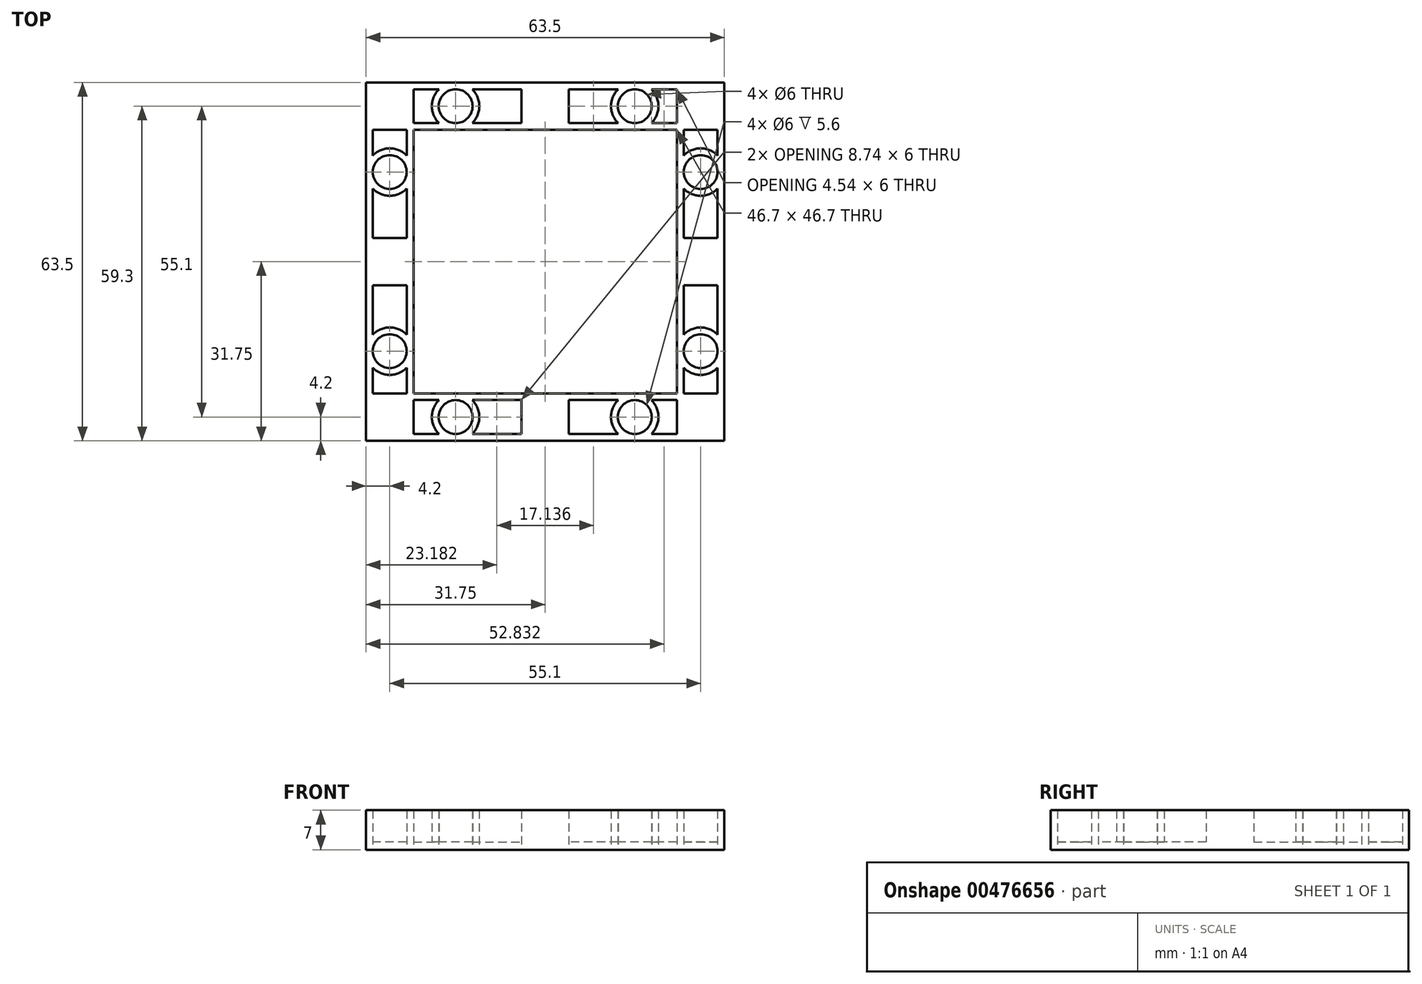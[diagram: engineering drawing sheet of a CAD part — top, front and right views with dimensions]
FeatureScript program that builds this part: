
annotation { "Feature Type Name" : "Feature", "Feature Type Description" : "" }
export const myFeature = defineFeature(function(context is Context, id is Id, definition is map)
    precondition{}
    {
        {
            var Q0;
            Q0=qCreatedBy(makeId("Top.planeOp"),FACE);
            var sketch = newSketch(context, id + "F0", { "sketchPlane" : qUnion([Q0])});
            skLineSegment(sketch, "E0", {"start": v(0, 31.75) * mm, "end": v(-31.75, 31.75) * mm});
            skLineSegment(sketch, "E1", {"start": v(-31.75, 31.75) * mm, "end": v(-31.75, 0) * mm});
            skLineSegment(sketch, "E2.0", {"start": v(-23.35, 23.35) * mm, "end": v(-23.35, 0) * mm});
            skLineSegment(sketch, "E2.1", {"start": v(0, 23.35) * mm, "end": v(-23.35, 23.35) * mm});
            skLineSegment(sketch, "E3.0", {"start": v(-30.55, 23.35) * mm, "end": v(-30.55, 18.81) * mm});
            skLineSegment(sketch, "E3.1", {"start": v(0, 30.55) * mm, "end": v(-12.94, 30.55) * mm});
            skLineSegment(sketch, "E4.0", {"start": v(-24.55, 23.35) * mm, "end": v(-24.55, 18.81) * mm});
            skLineSegment(sketch, "E4.1", {"start": v(0, 24.55) * mm, "end": v(-12.94, 24.55) * mm});
            skLineSegment(sketch, "E5", {"start": v(-23.35, 24.55) * mm, "end": v(-23.35, 30.55) * mm});
            skLineSegment(sketch, "E6", {"start": v(-24.55, 23.35) * mm, "end": v(-30.55, 23.35) * mm});
            skCircle(sketch, "E7", {"center": v(-15.88, 27.55) * mm, "radius": 3 * mm});
            skLineSegment(sketch, "E8", {"start": v(-4.2, 30.55) * mm, "end": v(-4.2, 24.55) * mm});
            skCircle(sketch, "E9", {"center": v(-27.55, 15.88) * mm, "radius": 3 * mm});
            skLineSegment(sketch, "E10", {"start": v(-30.55, 4.2) * mm, "end": v(-24.55, 4.2) * mm});
            skArc(sketch, "E11.0", {"start": v(-18.81, 30.55) * mm, "mid": v(-20.08, 27.55) * mm, "end": v(-18.81, 24.55) * mm});
            skArc(sketch, "E12.0", {"start": v(-24.55, 18.81) * mm, "mid": v(-27.55, 20.08) * mm, "end": v(-30.55, 18.81) * mm});
            skArc(sketch, "E13.trimOffspring", {"start": v(-12.94, 24.55) * mm, "mid": v(-11.68, 27.55) * mm, "end": v(-12.94, 30.55) * mm});
            skLineSegment(sketch, "E14.trimOffspring", {"start": v(-18.81, 24.55) * mm, "end": v(-23.35, 24.55) * mm});
            skLineSegment(sketch, "E15.trimOffspring", {"start": v(-18.81, 30.55) * mm, "end": v(-23.35, 30.55) * mm});
            skArc(sketch, "E16.trimOffspring", {"start": v(-30.55, 12.94) * mm, "mid": v(-27.55, 11.67) * mm, "end": v(-24.55, 12.94) * mm});
            skLineSegment(sketch, "E17.trimOffspring", {"start": v(-30.55, 12.94) * mm, "end": v(-30.55, 0) * mm});
            skLineSegment(sketch, "E18.trimOffspring", {"start": v(-24.55, 12.94) * mm, "end": v(-24.55, 0) * mm});
            skArc(sketch, "E19.MirrorCS", {"start": v(12.94, 24.55) * mm, "mid": v(11.68, 27.55) * mm, "end": v(12.94, 30.55) * mm});
            skLineSegment(sketch, "E20.MirrorCS", {"start": v(24.55, 12.94) * mm, "end": v(24.55, 0) * mm});
            skArc(sketch, "E21.MirrorCS", {"start": v(18.81, 30.55) * mm, "mid": v(20.08, 27.55) * mm, "end": v(18.81, 24.55) * mm});
            skArc(sketch, "E22.MirrorCS", {"start": v(24.55, 18.81) * mm, "mid": v(27.55, 20.08) * mm, "end": v(30.55, 18.81) * mm});
            skLineSegment(sketch, "E23.MirrorCS", {"start": v(0, 31.75) * mm, "end": v(31.75, 31.75) * mm});
            skLineSegment(sketch, "E24.MirrorCS", {"start": v(23.35, 23.35) * mm, "end": v(23.35, 0) * mm});
            skLineSegment(sketch, "E25.MirrorCS", {"start": v(0, 23.35) * mm, "end": v(23.35, 23.35) * mm});
            skLineSegment(sketch, "E26.MirrorCS", {"start": v(23.35, 24.55) * mm, "end": v(23.35, 30.55) * mm});
            skCircle(sketch, "E27.MirrorC", {"center": v(15.88, 27.55) * mm, "radius": 3 * mm});
            skLineSegment(sketch, "E28.MirrorCS", {"start": v(30.55, 12.94) * mm, "end": v(30.55, 0) * mm});
            skLineSegment(sketch, "E29.MirrorCS", {"start": v(4.2, 30.55) * mm, "end": v(4.2, 24.55) * mm});
            skLineSegment(sketch, "E30.MirrorCS", {"start": v(24.55, 23.35) * mm, "end": v(24.55, 18.81) * mm});
            skLineSegment(sketch, "E31.MirrorCS", {"start": v(0, 30.55) * mm, "end": v(12.94, 30.55) * mm});
            skLineSegment(sketch, "E32.MirrorCS", {"start": v(30.55, 23.35) * mm, "end": v(30.55, 18.81) * mm});
            skLineSegment(sketch, "E33.MirrorCS", {"start": v(18.81, 30.55) * mm, "end": v(23.35, 30.55) * mm});
            skCircle(sketch, "E34.MirrorC", {"center": v(27.55, 15.88) * mm, "radius": 3 * mm});
            skLineSegment(sketch, "E35.MirrorCS", {"start": v(24.55, 23.35) * mm, "end": v(30.55, 23.35) * mm});
            skLineSegment(sketch, "E36.MirrorCS", {"start": v(18.81, 24.55) * mm, "end": v(23.35, 24.55) * mm});
            skLineSegment(sketch, "E37.MirrorCS", {"start": v(31.75, 31.75) * mm, "end": v(31.75, 0) * mm});
            skLineSegment(sketch, "E38.MirrorCS", {"start": v(0, 24.55) * mm, "end": v(12.94, 24.55) * mm});
            skLineSegment(sketch, "E39.MirrorCS", {"start": v(30.55, 4.2) * mm, "end": v(24.55, 4.2) * mm});
            skArc(sketch, "E40.MirrorCS", {"start": v(30.55, 12.94) * mm, "mid": v(27.55, 11.67) * mm, "end": v(24.55, 12.94) * mm});
            skLineSegment(sketch, "E41.MirrorCS", {"start": v(0, -30.55) * mm, "end": v(12.94, -30.55) * mm});
            skLineSegment(sketch, "E42.MirrorCS", {"start": v(-18.81, -30.55) * mm, "end": v(-23.35, -30.55) * mm});
            skLineSegment(sketch, "E43.MirrorCS", {"start": v(24.55, -23.35) * mm, "end": v(30.55, -23.35) * mm});
            skLineSegment(sketch, "E44.MirrorCS", {"start": v(30.55, -12.94) * mm, "end": v(30.55, 0) * mm});
            skArc(sketch, "E45.MirrorCS", {"start": v(12.94, -24.55) * mm, "mid": v(11.68, -27.55) * mm, "end": v(12.94, -30.55) * mm});
            skArc(sketch, "E46.MirrorCS", {"start": v(24.55, -18.81) * mm, "mid": v(27.55, -20.08) * mm, "end": v(30.55, -18.81) * mm});
            skLineSegment(sketch, "E47.MirrorCS", {"start": v(0, -24.55) * mm, "end": v(12.94, -24.55) * mm});
            skLineSegment(sketch, "E48.MirrorCS", {"start": v(24.55, -23.35) * mm, "end": v(24.55, -18.81) * mm});
            skLineSegment(sketch, "E49.MirrorCS", {"start": v(-18.81, -24.55) * mm, "end": v(-23.35, -24.55) * mm});
            skCircle(sketch, "E50.MirrorC", {"center": v(27.55, -15.88) * mm, "radius": 3 * mm});
            skCircle(sketch, "E51.MirrorC", {"center": v(15.88, -27.55) * mm, "radius": 3 * mm});
            skLineSegment(sketch, "E52.MirrorCS", {"start": v(-24.55, -12.94) * mm, "end": v(-24.55, 0) * mm});
            skArc(sketch, "E53.MirrorCS", {"start": v(18.81, -30.55) * mm, "mid": v(20.08, -27.55) * mm, "end": v(18.81, -24.55) * mm});
            skLineSegment(sketch, "E54.MirrorCS", {"start": v(31.75, -31.75) * mm, "end": v(31.75, 0) * mm});
            skLineSegment(sketch, "E55.MirrorCS", {"start": v(0, -23.35) * mm, "end": v(23.35, -23.35) * mm});
            skLineSegment(sketch, "E56.MirrorCS", {"start": v(4.2, -30.55) * mm, "end": v(4.2, -24.55) * mm});
            skArc(sketch, "E57.MirrorCS", {"start": v(-12.94, -24.55) * mm, "mid": v(-11.68, -27.55) * mm, "end": v(-12.94, -30.55) * mm});
            skLineSegment(sketch, "E58.MirrorCS", {"start": v(18.81, -30.55) * mm, "end": v(23.35, -30.55) * mm});
            skLineSegment(sketch, "E59.MirrorCS", {"start": v(23.35, -24.55) * mm, "end": v(23.35, -30.55) * mm});
            skLineSegment(sketch, "E60.MirrorCS", {"start": v(-30.55, -12.94) * mm, "end": v(-30.55, 0) * mm});
            skLineSegment(sketch, "E61.MirrorCS", {"start": v(-31.75, -31.75) * mm, "end": v(-31.75, 0) * mm});
            skLineSegment(sketch, "E62.MirrorCS", {"start": v(24.55, -12.94) * mm, "end": v(24.55, 0) * mm});
            skArc(sketch, "E63.MirrorCS", {"start": v(-18.81, -30.55) * mm, "mid": v(-20.08, -27.55) * mm, "end": v(-18.81, -24.55) * mm});
            skLineSegment(sketch, "E64.MirrorCS", {"start": v(-30.55, -4.2) * mm, "end": v(-24.55, -4.2) * mm});
            skArc(sketch, "E65.MirrorCS", {"start": v(30.55, -12.94) * mm, "mid": v(27.55, -11.67) * mm, "end": v(24.55, -12.94) * mm});
            skCircle(sketch, "E66.MirrorC", {"center": v(-27.55, -15.88) * mm, "radius": 3 * mm});
            skLineSegment(sketch, "E67.MirrorCS", {"start": v(0, -31.75) * mm, "end": v(31.75, -31.75) * mm});
            skLineSegment(sketch, "E68.MirrorCS", {"start": v(30.55, -4.2) * mm, "end": v(24.55, -4.2) * mm});
            skLineSegment(sketch, "E69.MirrorCS", {"start": v(-24.55, -23.35) * mm, "end": v(-30.55, -23.35) * mm});
            skLineSegment(sketch, "E70.MirrorCS", {"start": v(-23.35, -24.55) * mm, "end": v(-23.35, -30.55) * mm});
            skLineSegment(sketch, "E71.MirrorCS", {"start": v(-23.35, -23.35) * mm, "end": v(-23.35, 0) * mm});
            skLineSegment(sketch, "E72.MirrorCS", {"start": v(30.55, -23.35) * mm, "end": v(30.55, -18.81) * mm});
            skLineSegment(sketch, "E73.MirrorCS", {"start": v(0, -30.55) * mm, "end": v(-12.94, -30.55) * mm});
            skLineSegment(sketch, "E74.MirrorCS", {"start": v(0, -24.55) * mm, "end": v(-12.94, -24.55) * mm});
            skLineSegment(sketch, "E75.MirrorCS", {"start": v(-30.55, -23.35) * mm, "end": v(-30.55, -18.81) * mm});
            skArc(sketch, "E76.MirrorCS", {"start": v(-24.55, -18.81) * mm, "mid": v(-27.55, -20.08) * mm, "end": v(-30.55, -18.81) * mm});
            skLineSegment(sketch, "E77.MirrorCS", {"start": v(0, -31.75) * mm, "end": v(-31.75, -31.75) * mm});
            skLineSegment(sketch, "E78.MirrorCS", {"start": v(0, -23.35) * mm, "end": v(-23.35, -23.35) * mm});
            skLineSegment(sketch, "E79.MirrorCS", {"start": v(-4.2, -30.55) * mm, "end": v(-4.2, -24.55) * mm});
            skCircle(sketch, "E80.MirrorC", {"center": v(-15.88, -27.55) * mm, "radius": 3 * mm});
            skLineSegment(sketch, "E81.MirrorCS", {"start": v(-24.55, -23.35) * mm, "end": v(-24.55, -18.81) * mm});
            skArc(sketch, "E82.MirrorCS", {"start": v(-30.55, -12.94) * mm, "mid": v(-27.55, -11.67) * mm, "end": v(-24.55, -12.94) * mm});
            skLineSegment(sketch, "E83.MirrorCS", {"start": v(18.81, -24.55) * mm, "end": v(23.35, -24.55) * mm});
            skLineSegment(sketch, "E84.MirrorCS", {"start": v(23.35, -23.35) * mm, "end": v(23.35, 0) * mm});
            skPoint(sketch, "E85.orphan", {"position": v(-31.75, 23.35) * mm});
            skPoint(sketch, "E86.orphan", {"position": v(31.75, 23.35) * mm});
            skPoint(sketch, "E87.orphan", {"position": v(-31.75, -23.35) * mm});
            skPoint(sketch, "E88.orphan", {"position": v(31.75, -23.35) * mm});
            skSolve(sketch);
        }
        {
            var Q0;
            Q0=makeQuery(id+"F0.imprint","IMPRINT",FACE,{"disambiguationData":[TD([[makeQuery(id+"F0.imprint","IMPRINT",EDGE,{"derivedFrom":sQuery(id+"F0.wireOp",EDGE,"E0")}),1.0]])]});
            var Q1;
            Q1=makeQuery(id+"F0.imprint","IMPRINT",FACE,{"disambiguationData":[TD([[makeQuery(id+"F0.imprint","IMPRINT",EDGE,{"derivedFrom":sQuery(id+"F0.wireOp",EDGE,"E3.0")}),1.0]])]});
            var Q2;
            Q2=makeQuery(id+"F0.imprint","IMPRINT",FACE,{"disambiguationData":[TD([[makeQuery(id+"F0.imprint","IMPRINT",EDGE,{"derivedFrom":sQuery(id+"F0.wireOp",EDGE,"E9")}),1.0]])]});
            var Q3;
            Q3=makeQuery(id+"F0.imprint","IMPRINT",FACE,{"disambiguationData":[TD([[makeQuery(id+"F0.imprint","IMPRINT",EDGE,{"derivedFrom":sQuery(id+"F0.wireOp",EDGE,"E7")}),1.0]])]});
            var Q4;
            Q4=makeQuery(id+"F0.imprint","IMPRINT",FACE,{"disambiguationData":[TD([[makeQuery(id+"F0.imprint","IMPRINT",EDGE,{"derivedFrom":sQuery(id+"F0.wireOp",EDGE,"E5")}),-1.0]])]});
            var Q5;
            {var subQ4=sQuery(id+"F0.wireOp",EDGE,"E8");Q5=makeQuery(id+"F0.imprint","IMPRINT",FACE,{"disambiguationData":[TD([[makeQuery(id+"F0.imprint","IMPRINT",EDGE,{"derivedFrom":subQ4}),1.0]])]});}
            var Q6;
            {var subQ2=sQuery(id+"F0.wireOp",EDGE,"E8");Q6=makeQuery(id+"F0.imprint","IMPRINT",FACE,{"disambiguationData":[TD([[makeQuery(id+"F0.imprint","IMPRINT",EDGE,{"derivedFrom":subQ2}),-1.0]])]});}
            var Q7;
            {var subQ0=sQuery(id+"F0.wireOp",EDGE,"E19.MirrorCS");Q7=makeQuery(id+"F0.imprint","IMPRINT",FACE,{"disambiguationData":[TD([[makeQuery(id+"F0.imprint","IMPRINT",EDGE,{"derivedFrom":subQ0}),1.0]])]});}
            var Q8;
            Q8=makeQuery(id+"F0.imprint","IMPRINT",FACE,{"disambiguationData":[TD([[makeQuery(id+"F0.imprint","IMPRINT",EDGE,{"derivedFrom":sQuery(id+"F0.wireOp",EDGE,"E27.MirrorC")}),-1.0]])]});
            var Q9;
            Q9=makeQuery(id+"F0.imprint","IMPRINT",FACE,{"disambiguationData":[TD([[makeQuery(id+"F0.imprint","IMPRINT",EDGE,{"derivedFrom":sQuery(id+"F0.wireOp",EDGE,"E21.MirrorCS")}),1.0]])]});
            var Q10;
            Q10=makeQuery(id+"F0.imprint","IMPRINT",FACE,{"disambiguationData":[TD([[makeQuery(id+"F0.imprint","IMPRINT",EDGE,{"derivedFrom":sQuery(id+"F0.wireOp",EDGE,"E22.MirrorCS")}),1.0]])]});
            var Q11;
            Q11=makeQuery(id+"F0.imprint","IMPRINT",FACE,{"disambiguationData":[TD([[makeQuery(id+"F0.imprint","IMPRINT",EDGE,{"derivedFrom":sQuery(id+"F0.wireOp",EDGE,"E34.MirrorC")}),-1.0]])]});
            var Q12;
            {var subQ2=sQuery(id+"F0.wireOp",EDGE,"E39.MirrorCS");Q12=makeQuery(id+"F0.imprint","IMPRINT",FACE,{"disambiguationData":[TD([[makeQuery(id+"F0.imprint","IMPRINT",EDGE,{"derivedFrom":subQ2}),-1.0]])]});}
            var Q13;
            {var subQ0=sQuery(id+"F0.wireOp",EDGE,"E39.MirrorCS");Q13=makeQuery(id+"F0.imprint","IMPRINT",FACE,{"disambiguationData":[TD([[makeQuery(id+"F0.imprint","IMPRINT",EDGE,{"derivedFrom":subQ0}),1.0]])]});}
            var Q14;
            {var subQ0=sQuery(id+"F0.wireOp",EDGE,"E65.MirrorCS");Q14=makeQuery(id+"F0.imprint","IMPRINT",FACE,{"disambiguationData":[TD([[makeQuery(id+"F0.imprint","IMPRINT",EDGE,{"derivedFrom":subQ0}),-1.0]])]});}
            var Q15;
            Q15=makeQuery(id+"F0.imprint","IMPRINT",FACE,{"disambiguationData":[TD([[makeQuery(id+"F0.imprint","IMPRINT",EDGE,{"derivedFrom":sQuery(id+"F0.wireOp",EDGE,"E50.MirrorC")}),1.0]])]});
            var Q16;
            Q16=makeQuery(id+"F0.imprint","IMPRINT",FACE,{"disambiguationData":[TD([[makeQuery(id+"F0.imprint","IMPRINT",EDGE,{"derivedFrom":sQuery(id+"F0.wireOp",EDGE,"E43.MirrorCS")}),1.0]])]});
            var Q17;
            Q17=makeQuery(id+"F0.imprint","IMPRINT",FACE,{"disambiguationData":[TD([[makeQuery(id+"F0.imprint","IMPRINT",EDGE,{"derivedFrom":sQuery(id+"F0.wireOp",EDGE,"E53.MirrorCS")}),-1.0]])]});
            var Q18;
            Q18=makeQuery(id+"F0.imprint","IMPRINT",FACE,{"disambiguationData":[TD([[makeQuery(id+"F0.imprint","IMPRINT",EDGE,{"derivedFrom":sQuery(id+"F0.wireOp",EDGE,"E51.MirrorC")}),1.0]])]});
            var Q19;
            {var subQ0=sQuery(id+"F0.wireOp",EDGE,"E45.MirrorCS");Q19=makeQuery(id+"F0.imprint","IMPRINT",FACE,{"disambiguationData":[TD([[makeQuery(id+"F0.imprint","IMPRINT",EDGE,{"derivedFrom":subQ0}),-1.0]])]});}
            var Q20;
            {var subQ0=sQuery(id+"F0.wireOp",EDGE,"E56.MirrorCS");Q20=makeQuery(id+"F0.imprint","IMPRINT",FACE,{"disambiguationData":[TD([[makeQuery(id+"F0.imprint","IMPRINT",EDGE,{"derivedFrom":subQ0}),1.0]])]});}
            var Q21;
            {var subQ0=sQuery(id+"F0.wireOp",EDGE,"E57.MirrorCS");Q21=makeQuery(id+"F0.imprint","IMPRINT",FACE,{"disambiguationData":[TD([[makeQuery(id+"F0.imprint","IMPRINT",EDGE,{"derivedFrom":subQ0}),1.0]])]});}
            var Q22;
            Q22=makeQuery(id+"F0.imprint","IMPRINT",FACE,{"disambiguationData":[TD([[makeQuery(id+"F0.imprint","IMPRINT",EDGE,{"derivedFrom":sQuery(id+"F0.wireOp",EDGE,"E42.MirrorCS")}),-1.0]])]});
            var Q23;
            Q23=makeQuery(id+"F0.imprint","IMPRINT",FACE,{"disambiguationData":[TD([[makeQuery(id+"F0.imprint","IMPRINT",EDGE,{"derivedFrom":sQuery(id+"F0.wireOp",EDGE,"E80.MirrorC")}),-1.0]])]});
            var Q24;
            Q24=makeQuery(id+"F0.imprint","IMPRINT",FACE,{"disambiguationData":[TD([[makeQuery(id+"F0.imprint","IMPRINT",EDGE,{"derivedFrom":sQuery(id+"F0.wireOp",EDGE,"E69.MirrorCS")}),-1.0]])]});
            var Q25;
            Q25=makeQuery(id+"F0.imprint","IMPRINT",FACE,{"disambiguationData":[TD([[makeQuery(id+"F0.imprint","IMPRINT",EDGE,{"derivedFrom":sQuery(id+"F0.wireOp",EDGE,"E66.MirrorC")}),-1.0]])]});
            var Q26;
            {var subQ2=sQuery(id+"F0.wireOp",EDGE,"E64.MirrorCS");Q26=makeQuery(id+"F0.imprint","IMPRINT",FACE,{"disambiguationData":[TD([[makeQuery(id+"F0.imprint","IMPRINT",EDGE,{"derivedFrom":subQ2}),-1.0]])]});}
            var Q27;
            {var subQ5=sQuery(id+"F0.wireOp",EDGE,"E10");Q27=makeQuery(id+"F0.imprint","IMPRINT",FACE,{"disambiguationData":[TD([[makeQuery(id+"F0.imprint","IMPRINT",EDGE,{"derivedFrom":subQ5}),-1.0]])]});}
            var Q28;
            {var subQ0=sQuery(id+"F0.wireOp",EDGE,"E10");Q28=makeQuery(id+"F0.imprint","IMPRINT",FACE,{"disambiguationData":[TD([[makeQuery(id+"F0.imprint","IMPRINT",EDGE,{"derivedFrom":subQ0}),1.0]])]});}
            extrude(context, id + "F1", {"entities" : qUnion([Q0, Q1, Q2, Q3, Q4, Q5, Q6, Q7, Q8, Q9, Q10, Q11, Q12, Q13, Q14, Q15, Q16, Q17, Q18, Q19, Q20, Q21, Q22, Q23, Q24, Q25, Q26, Q27, Q28]), "depth" : 1.4 * mm, "offsetDistance" : 25 * mm});
        }
        {
            var Q0;
            Q0=makeQuery(id+"F0.imprint","IMPRINT",FACE,{"disambiguationData":[TD([[makeQuery(id+"F0.imprint","IMPRINT",EDGE,{"derivedFrom":sQuery(id+"F0.wireOp",EDGE,"E0")}),1.0]])]});
            var Q1;
            {var subQ0=sQuery(id+"F0.wireOp",EDGE,"E56.MirrorCS");Q1=makeQuery(id+"F0.imprint","IMPRINT",FACE,{"disambiguationData":[TD([[makeQuery(id+"F0.imprint","IMPRINT",EDGE,{"derivedFrom":subQ0}),1.0]])]});}
            var Q2;
            {var subQ0=sQuery(id+"F0.wireOp",EDGE,"E39.MirrorCS");Q2=makeQuery(id+"F0.imprint","IMPRINT",FACE,{"disambiguationData":[TD([[makeQuery(id+"F0.imprint","IMPRINT",EDGE,{"derivedFrom":subQ0}),1.0]])]});}
            var Q3;
            {var subQ4=sQuery(id+"F0.wireOp",EDGE,"E8");Q3=makeQuery(id+"F0.imprint","IMPRINT",FACE,{"disambiguationData":[TD([[makeQuery(id+"F0.imprint","IMPRINT",EDGE,{"derivedFrom":subQ4}),1.0]])]});}
            var Q4;
            {var subQ5=sQuery(id+"F0.wireOp",EDGE,"E10");Q4=makeQuery(id+"F0.imprint","IMPRINT",FACE,{"disambiguationData":[TD([[makeQuery(id+"F0.imprint","IMPRINT",EDGE,{"derivedFrom":subQ5}),-1.0]])]});}
            extrude(context, id + "F2", {"entities" : qUnion([Q0, Q1, Q2, Q3, Q4]), "operationType" : NewBodyOperationType.ADD, "depth" : 7 * mm, "offsetDistance" : 25 * mm});
        }
    });
